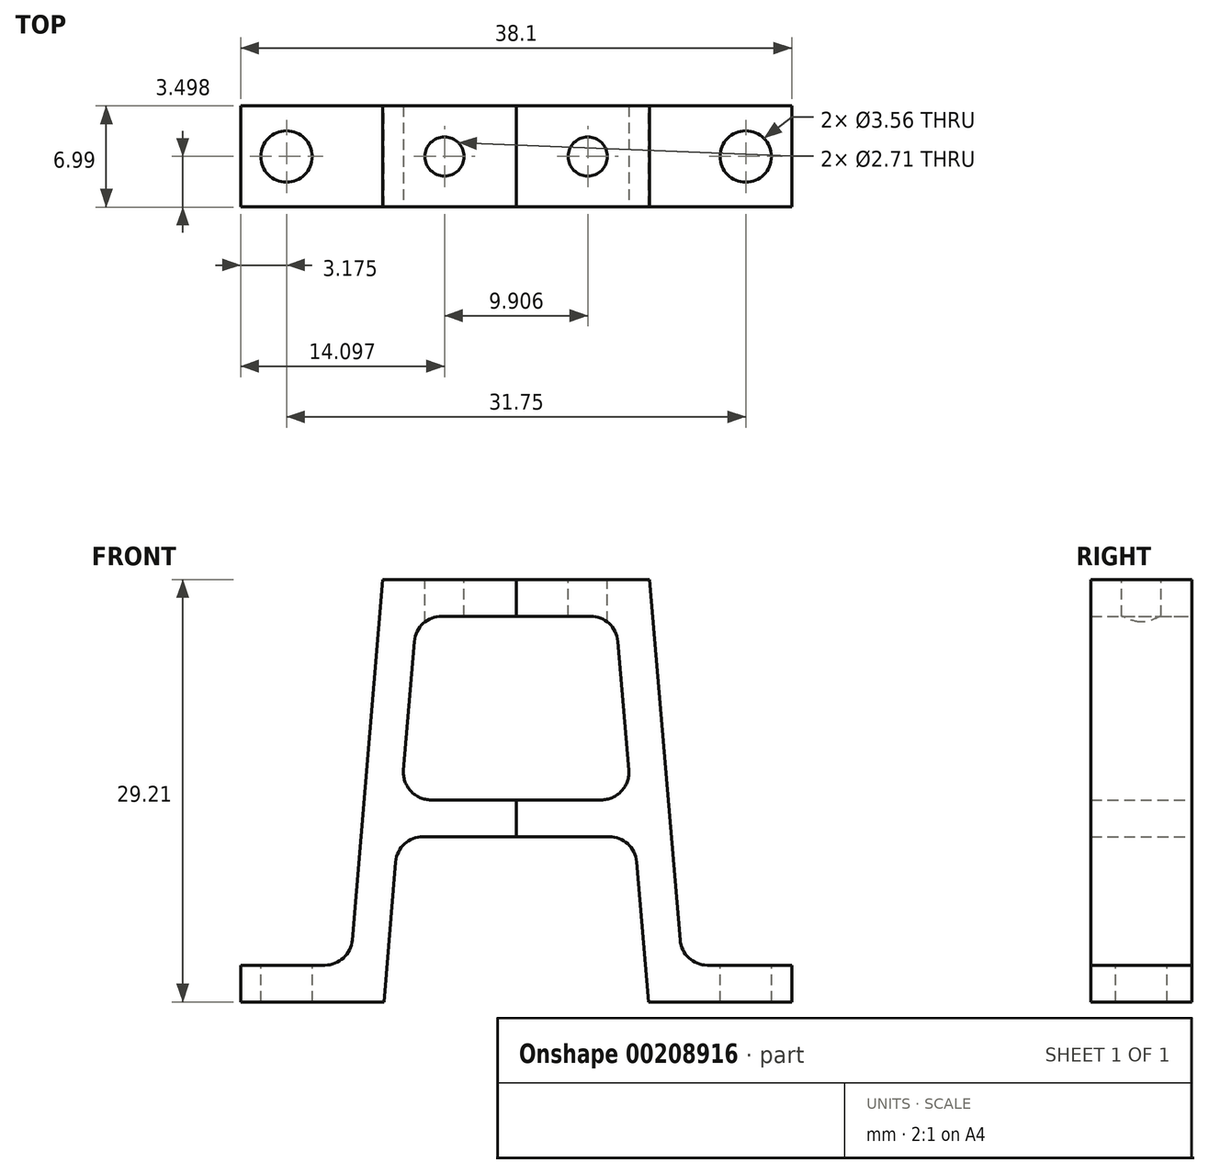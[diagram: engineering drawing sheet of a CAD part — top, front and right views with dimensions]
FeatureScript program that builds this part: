
annotation { "Feature Type Name" : "Feature", "Feature Type Description" : "" }
export const myFeature = defineFeature(function(context is Context, id is Id, definition is map)
    precondition{}
    {
        {
            var Q0;
            Q0=qCreatedBy(makeId("Front.planeOp"),FACE);
            var sketch = newSketch(context, id + "F0", { "sketchPlane" : qUnion([Q0])});
            skLineSegment(sketch, "E0", {"start": v(0, 29.2) * mm, "end": v(9.22, 29.2) * mm});
            skLineSegment(sketch, "E1", {"start": v(9.22, 29.21) * mm, "end": v(11.48, 2.54) * mm});
            skLineSegment(sketch, "E2", {"start": v(11.48, 2.54) * mm, "end": v(19.05, 2.54) * mm});
            skLineSegment(sketch, "E3", {"start": v(19.05, 2.54) * mm, "end": v(19.05, 0) * mm});
            skLineSegment(sketch, "E4", {"start": v(19.05, 0) * mm, "end": v(9.14, 0) * mm});
            skLineSegment(sketch, "E5", {"start": v(9.14, 0) * mm, "end": v(8.18, 11.43) * mm});
            skLineSegment(sketch, "E6", {"start": v(8.18, 11.43) * mm, "end": v(0, 11.43) * mm});
            skLineSegment(sketch, "E7", {"start": v(0, 11.43) * mm, "end": v(0, 13.97) * mm});
            skLineSegment(sketch, "E8", {"start": v(0, 13.97) * mm, "end": v(7.96, 13.97) * mm});
            skLineSegment(sketch, "E9", {"start": v(7.96, 13.97) * mm, "end": v(6.89, 26.67) * mm});
            skLineSegment(sketch, "E10", {"start": v(6.89, 26.67) * mm, "end": v(0, 26.67) * mm});
            skLineSegment(sketch, "E11", {"start": v(0, 26.67) * mm, "end": v(0, 29.2) * mm});
            skPoint(sketch, "E12", {"position": v(0, 12.7) * mm});
            skLineSegment(sketch, "E13", {"start": v(7.42, 20.32) * mm, "end": v(9.95, 20.53) * mm});
            skSolve(sketch);
        }
        {
            var Q0;
            Q0=qSketchRegion(id+"F0",true);
            extrude(context, id + "F1", {"entities" : qUnion([Q0]), "depth" : 7 * mm});
        }
        {
            var Q0;
            Q0=makeQuery(id+"F1.opExtrude","SWEPT_EDGE",EDGE,{"disambiguationData":[OSD([sQuery(id+"F0.wireOp",EDGE,"E1"),sQuery(id+"F0.wireOp",EDGE,"E2")])]});
            var Q1;
            Q1=makeQuery(id+"F1.opExtrude","SWEPT_EDGE",EDGE,{"disambiguationData":[OSD([sQuery(id+"F0.wireOp",EDGE,"E5"),sQuery(id+"F0.wireOp",EDGE,"E6")])]});
            var Q2;
            Q2=makeQuery(id+"F1.opExtrude","SWEPT_EDGE",EDGE,{"disambiguationData":[OSD([sQuery(id+"F0.wireOp",EDGE,"E9"),sQuery(id+"F0.wireOp",EDGE,"E10")])]});
            var Q3;
            Q3=makeQuery(id+"F1.opExtrude","SWEPT_EDGE",EDGE,{"disambiguationData":[OSD([sQuery(id+"F0.wireOp",EDGE,"E8"),sQuery(id+"F0.wireOp",EDGE,"E9")])]});
            fillet(context, id + "F2", {"entities" : qUnion([Q0, Q1, Q2, Q3]), "radius" : 1.9 * mm, "tangentPropagation" : true, "allowEdgeOverflow" : false});
        }
        {
            var Q0;
            Q0=makeQuery(id+"F1.opExtrude","SWEPT_FACE",FACE,{"disambiguationData":[OSD([sQuery(id+"F0.wireOp",EDGE,"E2")])]});
            var sketch = newSketch(context, id + "F3", { "sketchPlane" : qUnion([Q0])});
            skCircle(sketch, "E14", {"center": v(15.88, -3.5) * mm, "radius": 1.78 * mm});
            skPoint(sketch, "E15", {"position": v(19.05, -3.5) * mm});
            skSolve(sketch);
        }
        {
            var Q0;
            Q0=qSketchRegion(id+"F3",true);
            extrude(context, id + "F4", {"entities" : qUnion([Q0]), "operationType" : NewBodyOperationType.REMOVE, "endBound" : BoundingType.UP_TO_NEXT, "oppositeDirection" : true, "depth" : 25.4 * mm});
        }
        {
            var Q0;
            Q0=makeQuery(id+"F1.opExtrude","SWEPT_FACE",FACE,{"disambiguationData":[OSD([sQuery(id+"F0.wireOp",EDGE,"E0")])]});
            var sketch = newSketch(context, id + "F5", { "sketchPlane" : qUnion([Q0])});
            skCircle(sketch, "E16", {"center": v(4.95, -3.5) * mm, "radius": 1.35 * mm});
            skPoint(sketch, "E17", {"position": v(9.22, -3.5) * mm});
            skSolve(sketch);
        }
        {
            var Q0;
            Q0=qSketchRegion(id+"F5",true);
            extrude(context, id + "F6", {"entities" : qUnion([Q0]), "operationType" : NewBodyOperationType.REMOVE, "endBound" : BoundingType.UP_TO_NEXT, "oppositeDirection" : true, "depth" : 25.4 * mm});
        }
        {
            var Q0;
            Q0=makeQuery(id+"F1.opExtrude","SWEPT_BODY",BODY,{"disambiguationData":[OSD([sQuery(id+"F0.wireOp",EDGE,"E0"),sQuery(id+"F0.wireOp",EDGE,"E1"),sQuery(id+"F0.wireOp",EDGE,"E2"),sQuery(id+"F0.wireOp",EDGE,"E3"),sQuery(id+"F0.wireOp",EDGE,"E4"),sQuery(id+"F0.wireOp",EDGE,"E5"),sQuery(id+"F0.wireOp",EDGE,"E6"),sQuery(id+"F0.wireOp",EDGE,"E7"),sQuery(id+"F0.wireOp",EDGE,"E8"),sQuery(id+"F0.wireOp",EDGE,"E9"),sQuery(id+"F0.wireOp",EDGE,"E10"),sQuery(id+"F0.wireOp",EDGE,"E11")])]});
            var Q1;
            Q1=qCreatedBy(makeId("Right.planeOp"),FACE);
            mirror(context, id + "F7", {"entities" : qUnion([Q0]), "mirrorPlane" : qUnion([Q1])});
        }
    });
